# Revit family: 0047251
name_source: partatom
category: Lighting Fixtures
revit_build: Autodesk Revit 2017 (Build: 20160225_1515(x64)
units: mm (PartAtom-declared; Revit-internal decimal feet)

## family parameters
Cut with Voids When Loaded = No
Host = Face
Light Source = Yes
OmniClass Number = 23.80.70.00
OmniClass Title = Lighting
Part Type = Normal
Room Calculation Point = No
Round Connector Dimension = Use Diameter
Shared = No

## types (8) — shared parameters
Assembly Code = D5020200
ClassificationName = Uniclass2015
ClassificationValue = EF_70_80
Color Filter = 16777215
Default Elevation = 1219 mm
Dimming Lamp Color Temperature Shift = <None>
ElectricShockClassification = Class II
Emit Shape Visible in Rendering = No
Emit from Rectangle Length = 525 mm
Emit from Rectangle Width = 525 mm
IfcExportAs = IfcLightFixtureType
IfcExportType = IfcLightFixtureType
ImpactProtectionIndex = IK08
IngressProtection = IP20
InputNominalFrequency = 50/60 Hz
InputVoltage = 220-240 V AC
Keynote = 16500
Lamp = LED
LampColourTemperature = 3000 K
LampsType = LED
LuminaireType = panel
Manufacturer = Feilo Sylvania
ManufacturerName = Feilo Sylvania
Material_1_SYL = Body-Matrix-wh
Material_2_SYL = <By Category>
Material_3_SYL = <By Category>
Material_4_SYL = <By Category>
ModelNumber = 0047251
NominalDepth = 595 mm  [stored 1.9521 ft]
NominalHeight = 10 mm  [stored 0.0328084 ft]
NominalLength = 595 mm  [stored 1.9521 ft]
Tilt Angle = -90.00°
Type Image = <None>
URL = http://www.sylvania-lighting.com
Voltage = 230 V
Width_SYL = 595 mm  [stored 1.9521 ft]
zero-valued in all types: Cost, PowerFactor

## per-type parameters (varying)
| type | Apparent Load | LampNominalLuminous | LuminousEfficacy | Model | ModelReference | Name | Photometric Web File | PowerConsumption | TypeName |
| 0047251 Quadro UGR16 600 MPOWER 2050-4500LM 840 - 34W | 34 VA | 4444 lm | 131.49 lm/W | Quadro UGR16 600 MPOWER 2050-4500LM 840 - 34W | Quadro UGR16 600 MPOWER 2050-4500LM 840 - 34W | Quadro UGR16 600 MPOWER 2050-4500LM 840 - 34W | 0047251_34W.ies | 33.8 W | Quadro UGR16 600 MPOWER 2050-4500LM 840 - 34W |
| 0047251 Quadro UGR16 600 MPOWER 2050-4500LM 840 - 32W | 32 VA | 4498 lm | 139.27 lm/W | Quadro UGR16 600 MPOWER 2050-4500LM 840 - 32W | Quadro UGR16 600 MPOWER 2050-4500LM 840 - 32W | Quadro UGR16 600 MPOWER 2050-4500LM 840 - 32W | 0047251_32W.ies | 32.3 W | Quadro UGR16 600 MPOWER 2050-4500LM 840 - 32W |
| 0047251 Quadro UGR16 600 MPOWER 2050-4500LM 840 - 30W | 29 VA | 4328 lm | 147.73 lm/W | Quadro UGR16 600 MPOWER 2050-4500LM 840 - 30W | Quadro UGR16 600 MPOWER 2050-4500LM 840 - 30W | Quadro UGR16 600 MPOWER 2050-4500LM 840 - 30W | 0047251_30W.ies | 29.3 W | Quadro UGR16 600 MPOWER 2050-4500LM 840 - 30W |
| 0047251 Quadro UGR16 600 MPOWER 2050-4500LM 840 - 27W | 27 VA | 3993 lm | 149.01 lm/W | Quadro UGR16 600 MPOWER 2050-4500LM 840 - 27W | Quadro UGR16 600 MPOWER 2050-4500LM 840 - 27W | Quadro UGR16 600 MPOWER 2050-4500LM 840 - 27W | 0047251_27W.ies | 26.8 W | Quadro UGR16 600 MPOWER 2050-4500LM 840 - 27W |
| 0047251 Quadro UGR16 600 MPOWER 2050-4500LM 840 - 24W | 23 VA | 3697 lm | 158.68 lm/W | Quadro UGR16 600 MPOWER 2050-4500LM 840 - 24W | Quadro UGR16 600 MPOWER 2050-4500LM 840 - 24W | Quadro UGR16 600 MPOWER 2050-4500LM 840 - 24W | 0047251_24W.ies | 23.3 W | Quadro UGR16 600 MPOWER 2050-4500LM 840 - 24W |
| 0047251 Quadro UGR16 600 MPOWER 2050-4500LM 840 - 21W | 21 VA | 3275 lm | 159.01 lm/W | Quadro UGR16 600 MPOWER 2050-4500LM 840 - 21W | Quadro UGR16 600 MPOWER 2050-4500LM 840 - 21W | Quadro UGR16 600 MPOWER 2050-4500LM 840 - 21W | 0047251_21W.ies | 20.6 W | Quadro UGR16 600 MPOWER 2050-4500LM 840 - 21W |
| 0047251 Quadro UGR16 600 MPOWER 2050-4500LM 840 - 18W | 17 VA | 2460 lm | 146.44 lm/W | Quadro UGR16 600 MPOWER 2050-4500LM 840 - 18W | Quadro UGR16 600 MPOWER 2050-4500LM 840 - 18W | Quadro UGR16 600 MPOWER 2050-4500LM 840 - 18W | 0047251_18W.ies | 16.8 W | Quadro UGR16 600 MPOWER 2050-4500LM 840 - 18W |
| 0047251 Quadro UGR16 600 MPOWER 2050-4500LM 840 - 15W | 14 VA | 2424 lm | 173.19 lm/W | Quadro UGR16 600 MPOWER 2050-4500LM 840 - 15W | Quadro UGR16 600 MPOWER 2050-4500LM 840 - 15W | Quadro UGR16 600 MPOWER 2050-4500LM 840 - 15W | 0047251_15W.ies | 14 W | Quadro UGR16 600 MPOWER 2050-4500LM 840 - 15W |

note: [stored X ft] marks values corroborated as IEEE doubles in the binary element streams (Revit-internal decimal feet)

## geometry (parser evidence)
native form markers: Sweep x4
no freeform markers — native parametric forms only
